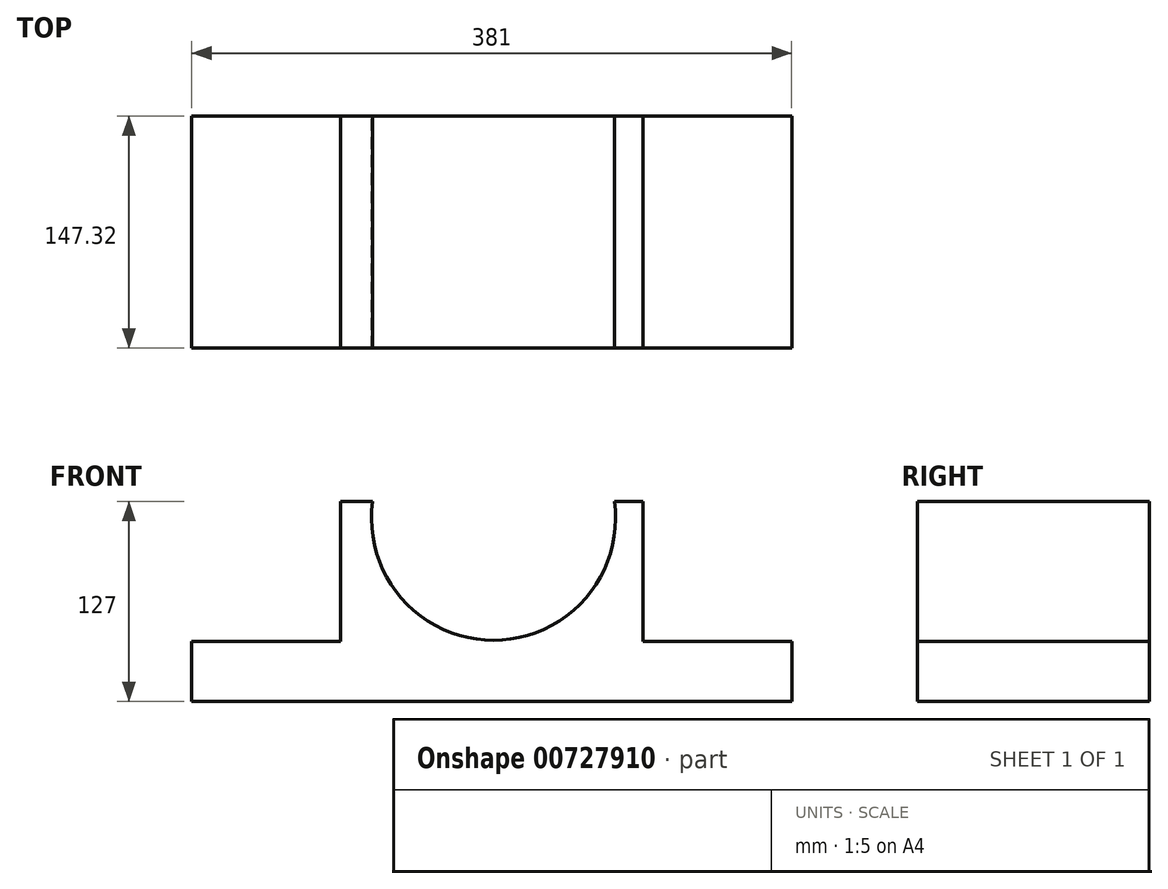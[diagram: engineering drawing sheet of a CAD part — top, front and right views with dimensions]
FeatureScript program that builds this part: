
annotation { "Feature Type Name" : "Feature", "Feature Type Description" : "" }
export const myFeature = defineFeature(function(context is Context, id is Id, definition is map)
    precondition{}
    {
        {
            var Q0;
            Q0=qCreatedBy(makeId("Front.planeOp"),FACE);
            var sketch = newSketch(context, id + "F0", { "sketchPlane" : qUnion([Q0])});
            skLineSegment(sketch, "E0", {"start": v(-189.34, -11.98) * mm, "end": v(191.66, -11.98) * mm});
            skLineSegment(sketch, "E1", {"start": v(191.66, -11.98) * mm, "end": v(191.66, 26.12) * mm});
            skLineSegment(sketch, "E2", {"start": v(-189.34, -11.98) * mm, "end": v(-189.34, 26.12) * mm});
            skLineSegment(sketch, "E3", {"start": v(-189.34, 26.12) * mm, "end": v(-94.85, 26.12) * mm});
            skLineSegment(sketch, "E4", {"start": v(191.66, 26.12) * mm, "end": v(97.17, 26.12) * mm});
            skLineSegment(sketch, "E5", {"start": v(-94.85, 26.12) * mm, "end": v(-94.85, 115.02) * mm});
            skLineSegment(sketch, "E6", {"start": v(97.17, 26.12) * mm, "end": v(97.17, 115.02) * mm});
            skArc(sketch, "E7", {"start": v(-74.5, 115.02) * mm, "mid": v(2.3, 26.87) * mm, "end": v(79.08, 115.02) * mm});
            skLineSegment(sketch, "E8", {"start": v(-94.85, 115.02) * mm, "end": v(-74.5, 115.02) * mm});
            skLineSegment(sketch, "E9", {"start": v(79.08, 115.02) * mm, "end": v(97.17, 115.02) * mm});
            skSolve(sketch);
        }
        {
            var Q0;
            Q0=makeQuery(id+"F0.imprint","IMPRINT",FACE,{"disambiguationData":[TD([[makeQuery(id+"F0.imprint","IMPRINT",EDGE,{"derivedFrom":sQuery(id+"F0.wireOp",EDGE,"E0")}),1.0]])]});
            extrude(context, id + "F1", {"entities" : qUnion([Q0]), "depth" : 147.32 * mm, "offsetDistance" : 25.4 * mm});
        }
    });
